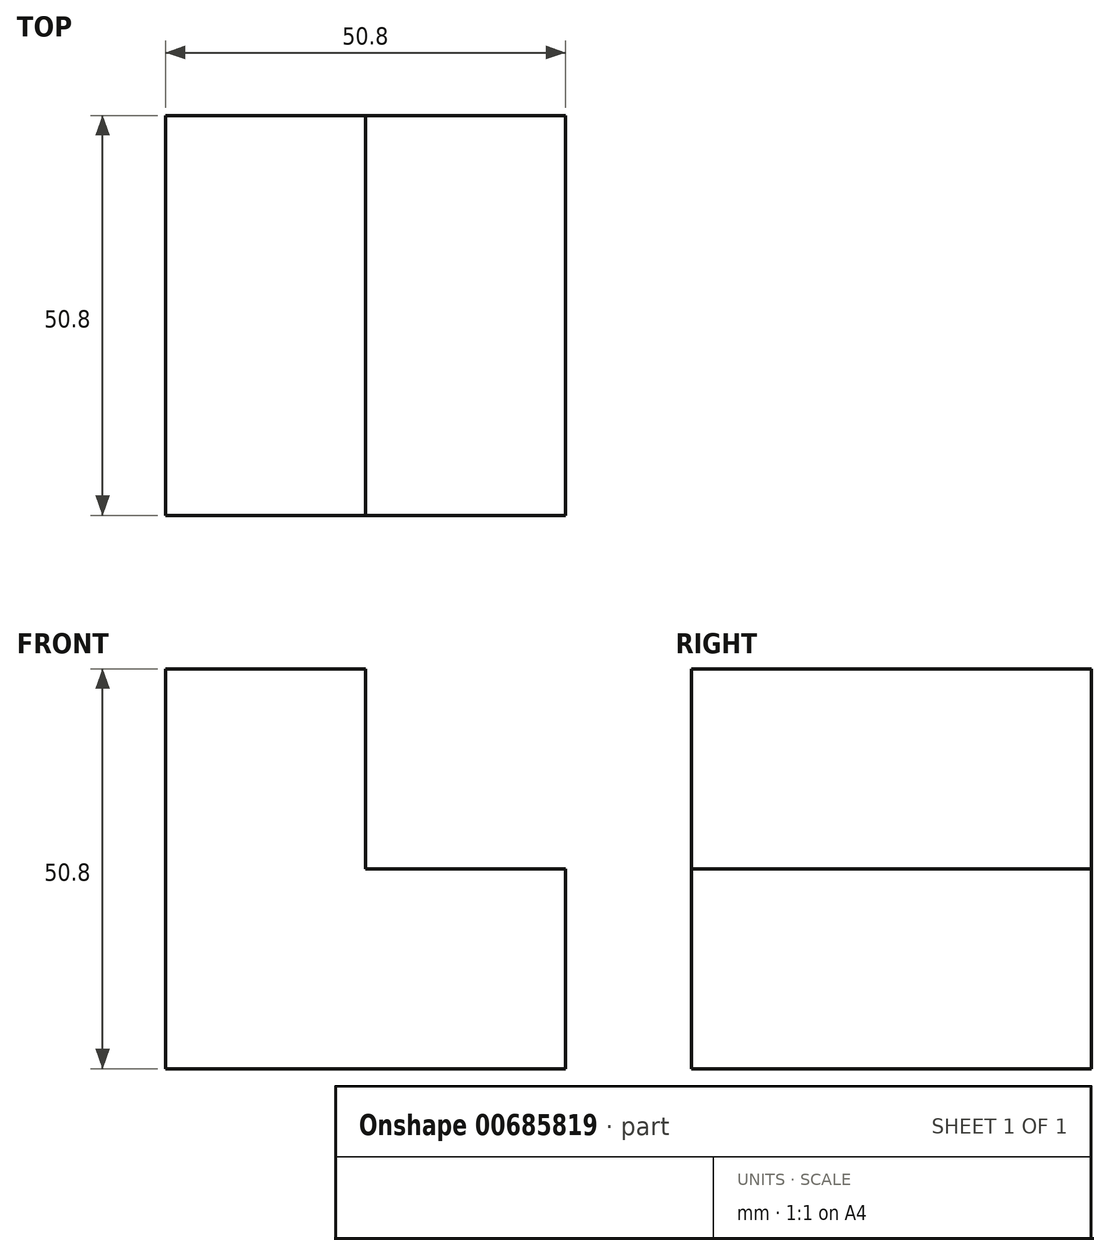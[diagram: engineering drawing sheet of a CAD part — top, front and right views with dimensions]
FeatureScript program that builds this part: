
annotation { "Feature Type Name" : "Feature", "Feature Type Description" : "" }
export const myFeature = defineFeature(function(context is Context, id is Id, definition is map)
    precondition{}
    {
        {
            var Q0;
            Q0=qCreatedBy(makeId("Front.planeOp"),FACE);
            var sketch = newSketch(context, id + "F0", { "sketchPlane" : qUnion([Q0])});
            skLineSegment(sketch, "E0", {"start": v(-36, 31.42) * mm, "end": v(-36, -19.38) * mm});
            skLineSegment(sketch, "E1", {"start": v(-36, -19.38) * mm, "end": v(14.8, -19.38) * mm});
            skLineSegment(sketch, "E2", {"start": v(-36, 31.42) * mm, "end": v(-10.6, 31.42) * mm});
            skLineSegment(sketch, "E3", {"start": v(-10.6, 31.42) * mm, "end": v(-10.6, 6.02) * mm});
            skLineSegment(sketch, "E4", {"start": v(-10.6, 6.02) * mm, "end": v(14.8, 6.02) * mm});
            skLineSegment(sketch, "E5", {"start": v(14.8, 6.02) * mm, "end": v(14.8, -19.38) * mm});
            skSolve(sketch);
        }
        {
            var Q0;
            Q0=makeQuery(id+"F0.imprint","IMPRINT",FACE,{"disambiguationData":[TD([[makeQuery(id+"F0.imprint","IMPRINT",EDGE,{"derivedFrom":sQuery(id+"F0.wireOp",EDGE,"E0")}),1.0]])]});
            extrude(context, id + "F1", {"entities" : qUnion([Q0]), "depth" : 50.8 * mm, "offsetDistance" : 25.4 * mm});
        }
    });
